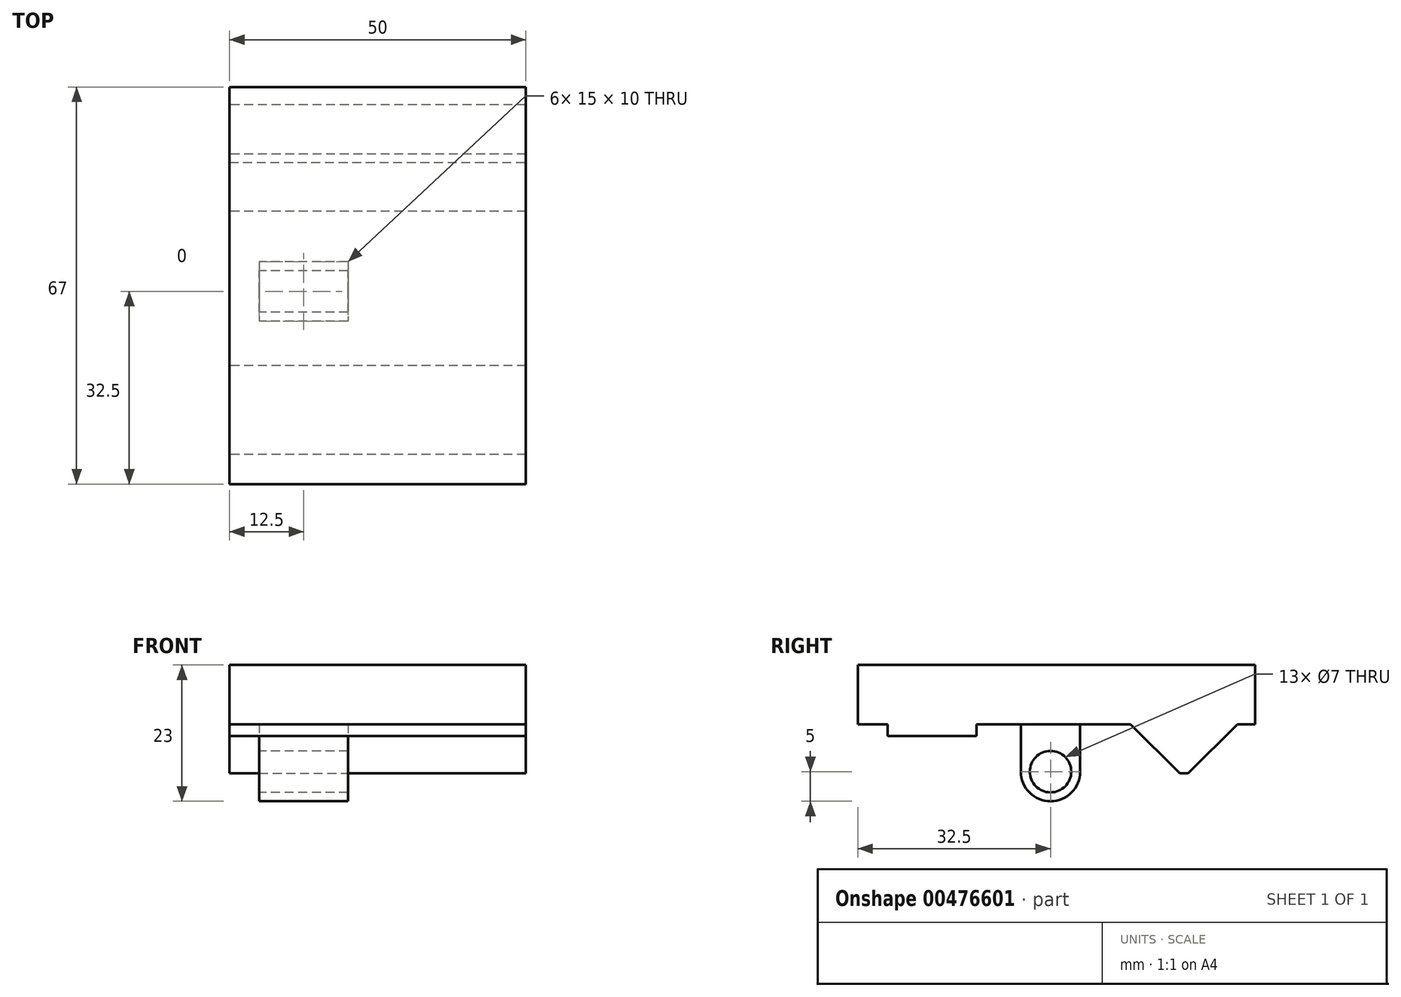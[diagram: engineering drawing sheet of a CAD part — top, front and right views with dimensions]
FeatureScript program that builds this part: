
annotation { "Feature Type Name" : "Feature", "Feature Type Description" : "" }
export const myFeature = defineFeature(function(context is Context, id is Id, definition is map)
    precondition{}
    {
        {
            var Q0;
            Q0=qCreatedBy(makeId("Right.planeOp"),FACE);
            var sketch = newSketch(context, id + "F0", { "sketchPlane" : qUnion([Q0])});
            skLineSegment(sketch, "E0.bottom", {"start": v(33.29, 6) * mm, "end": v(-33.71, 6) * mm});
            skLineSegment(sketch, "E0.top", {"start": v(33.29, -4) * mm, "end": v(30.29, -4) * mm});
            skLineSegment(sketch, "E0.left", {"start": v(33.29, 6) * mm, "end": v(33.29, -4) * mm});
            skLineSegment(sketch, "E0.right", {"start": v(-33.71, 6) * mm, "end": v(-33.71, -4) * mm});
            skLineSegment(sketch, "E1", {"start": v(12.29, -4) * mm, "end": v(21.29, -13) * mm});
            skLineSegment(sketch, "E2", {"start": v(21.29, -13) * mm, "end": v(30.29, -4) * mm});
            skLineSegment(sketch, "E3", {"start": v(-28.71, -4) * mm, "end": v(-28.71, -6) * mm});
            skLineSegment(sketch, "E4", {"start": v(-28.71, -6) * mm, "end": v(-13.71, -6) * mm});
            skLineSegment(sketch, "E5", {"start": v(-13.71, -6) * mm, "end": v(-13.71, -4) * mm});
            skArc(sketch, "E6", {"start": v(-6.21, -12) * mm, "mid": v(-1.21, -17) * mm, "end": v(3.79, -12) * mm});
            skLineSegment(sketch, "E7", {"start": v(-6.21, -12) * mm, "end": v(-6.21, -4) * mm});
            skLineSegment(sketch, "E8", {"start": v(3.79, -12) * mm, "end": v(3.79, -4) * mm});
            skLineSegment(sketch, "E9.trimOffspring", {"start": v(-28.71, -4) * mm, "end": v(-33.71, -4) * mm});
            skLineSegment(sketch, "E10.trimOffspring", {"start": v(-6.21, -4) * mm, "end": v(-13.71, -4) * mm});
            skLineSegment(sketch, "E11.trimOffspring", {"start": v(12.29, -4) * mm, "end": v(3.79, -4) * mm});
            skLineSegment(sketch, "E12", {"start": v(21.29, 18.04) * mm, "end": v(21.29, -34.07) * mm, "construction": true});
            skLineSegment(sketch, "E13", {"start": v(-21.21, 17.76) * mm, "end": v(-21.21, -31.4) * mm, "construction": true});
            skCircle(sketch, "E14", {"center": v(-1.21, -12) * mm, "radius": 3.5 * mm});
            skSolve(sketch);
        }
        {
            var Q0;
            Q0=makeQuery(id+"F0.imprint","IMPRINT",FACE,{"disambiguationData":[TD([[makeQuery(id+"F0.imprint","IMPRINT",EDGE,{"derivedFrom":sQuery(id+"F0.wireOp",EDGE,"E0.bottom")}),1.0]])]});
            extrude(context, id + "F1", {"entities" : qUnion([Q0]), "depth" : 50 * mm});
        }
        {
            var Q0;
            Q0=makeQuery(id+"F1.opExtrude","SWEPT_EDGE",EDGE,{"disambiguationData":[OSD([sQuery(id+"F0.wireOp",EDGE,"E1"),sQuery(id+"F0.wireOp",EDGE,"E2")])]});
            chamfer(context, id + "F2", {"entities" : qUnion([Q0]), "width" : 1 * mm, "tangentPropagation" : true});
        }
        {
            var Q0;
            Q0=makeQuery(id+"F1.opExtrude","SWEPT_FACE",FACE,{"disambiguationData":[OSD([sQuery(id+"F0.wireOp",EDGE,"E7")])]});
            var sketch = newSketch(context, id + "F3", { "sketchPlane" : qUnion([Q0])});
            skLineSegment(sketch, "E15.bottom", {"start": v(20, -4) * mm, "end": v(79.84, -4) * mm});
            skLineSegment(sketch, "E15.top", {"start": v(20, -31.45) * mm, "end": v(79.84, -31.45) * mm});
            skLineSegment(sketch, "E15.left", {"start": v(20, -4) * mm, "end": v(20, -31.45) * mm});
            skLineSegment(sketch, "E15.right", {"start": v(79.84, -4) * mm, "end": v(79.84, -31.45) * mm});
            skLineSegment(sketch, "E16.bottom", {"start": v(5, -4) * mm, "end": v(-35.27, -4) * mm});
            skLineSegment(sketch, "E16.top", {"start": v(5, -31.52) * mm, "end": v(-35.27, -31.52) * mm});
            skLineSegment(sketch, "E16.left", {"start": v(5, -4) * mm, "end": v(5, -31.52) * mm});
            skLineSegment(sketch, "E16.right", {"start": v(-35.27, -4) * mm, "end": v(-35.27, -31.52) * mm});
            skSolve(sketch);
        }
        {
            var Q0;
            {var subQ1=sQuery(id+"F0.wireOp",EDGE,"E7");var subQ2=makeQuery(id+"F1.opExtrude","CAP_EDGE",EDGE,{"disambiguationData":[OSD([subQ1])],"isStart":false});Q0=makeQuery(id+"F3.imprint","IMPRINT",FACE,{"disambiguationData":[TD([[makeQuery(id+"F3.imprint","IMPRINT",EDGE,{"derivedFrom":subQ2}),1.0]])]});}
            var Q1;
            {var subQ6=sQuery(id+"F3.wireOp",EDGE,"E15.top");Q1=makeQuery(id+"F3.imprint","IMPRINT",FACE,{"disambiguationData":[TD([[makeQuery(id+"F3.imprint","IMPRINT",EDGE,{"derivedFrom":subQ6}),1.0]])]});}
            var Q2;
            {var subQ1=sQuery(id+"F0.wireOp",EDGE,"E7");var subQ2=makeQuery(id+"F1.opExtrude","CAP_EDGE",EDGE,{"disambiguationData":[OSD([subQ1])],"isStart":true});Q2=makeQuery(id+"F3.imprint","IMPRINT",FACE,{"disambiguationData":[TD([[makeQuery(id+"F3.imprint","IMPRINT",EDGE,{"derivedFrom":subQ2}),-1.0]])]});}
            var Q3;
            {var subQ1=sQuery(id+"F3.wireOp",EDGE,"E16.top");Q3=makeQuery(id+"F3.imprint","IMPRINT",FACE,{"disambiguationData":[TD([[makeQuery(id+"F3.imprint","IMPRINT",EDGE,{"derivedFrom":subQ1}),-1.0]])]});}
            var Q4;
            Q4=makeQuery(id+"F1.opExtrude","SWEPT_FACE",FACE,{"disambiguationData":[OSD([sQuery(id+"F0.wireOp",EDGE,"E8")])]});
            extrude(context, id + "F4", {"entities" : qUnion([Q0, Q1, Q2, Q3]), "operationType" : NewBodyOperationType.REMOVE, "endBound" : BoundingType.UP_TO_SURFACE, "oppositeDirection" : true, "endBoundEntityFace" : qUnion([Q4]), "depth" : 25 * mm});
        }
    });
